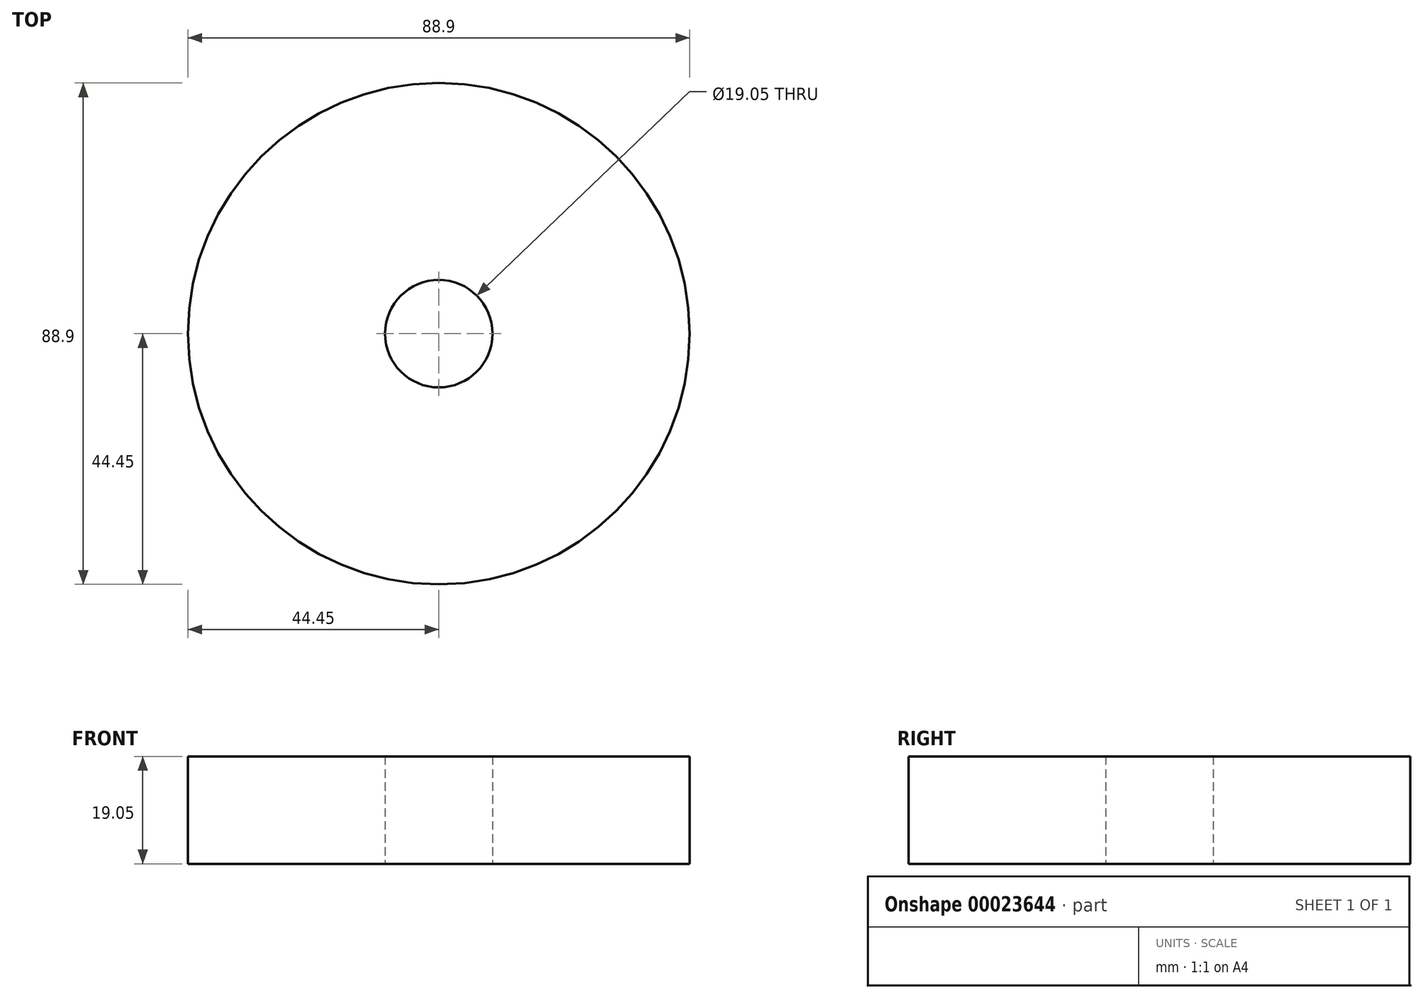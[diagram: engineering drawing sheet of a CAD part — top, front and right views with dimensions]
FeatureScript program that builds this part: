
annotation { "Feature Type Name" : "Feature", "Feature Type Description" : "" }
export const myFeature = defineFeature(function(context is Context, id is Id, definition is map)
    precondition{}
    {
        {
            var Q0;
            Q0=qCreatedBy(makeId("Front.planeOp"),FACE);
            var sketch = newSketch(context, id + "F0", { "sketchPlane" : qUnion([Q0])});
            skLineSegment(sketch, "E0", {"start": v(0, 0) * mm, "end": v(0, 75) * mm, "construction": true});
            skLineSegment(sketch, "E1.bottom", {"start": v(-9.52, 4.98) * mm, "end": v(-44.45, 4.98) * mm});
            skLineSegment(sketch, "E1.top", {"start": v(-9.53, 24.03) * mm, "end": v(-44.45, 24.03) * mm});
            skLineSegment(sketch, "E1.left", {"start": v(-9.53, 4.98) * mm, "end": v(-9.53, 24.03) * mm});
            skLineSegment(sketch, "E1.right", {"start": v(-44.45, 4.98) * mm, "end": v(-44.45, 24.03) * mm});
            skLineSegment(sketch, "E2.bottom", {"start": v(-9.53, 24.03) * mm, "end": v(-25.4, 24.03) * mm});
            skLineSegment(sketch, "E2.top", {"start": v(-9.53, 81.18) * mm, "end": v(-25.4, 81.18) * mm});
            skLineSegment(sketch, "E2.left", {"start": v(-9.53, 24.03) * mm, "end": v(-9.53, 81.18) * mm});
            skLineSegment(sketch, "E2.right", {"start": v(-25.4, 24.03) * mm, "end": v(-25.4, 81.18) * mm});
            skLineSegment(sketch, "E3.bottom", {"start": v(-9.53, 81.18) * mm, "end": v(-19.05, 81.18) * mm});
            skLineSegment(sketch, "E3.top", {"start": v(-9.53, 93.88) * mm, "end": v(-19.05, 93.88) * mm});
            skLineSegment(sketch, "E3.left", {"start": v(-9.53, 81.18) * mm, "end": v(-9.53, 93.88) * mm});
            skLineSegment(sketch, "E3.right", {"start": v(-19.05, 81.18) * mm, "end": v(-19.05, 93.88) * mm});
            skSolve(sketch);
        }
        {
            var Q0;
            Q0=makeQuery(id+"F0.imprint","IMPRINT",FACE,{"disambiguationData":[TD([[makeQuery(id+"F0.imprint","IMPRINT",EDGE,{"derivedFrom":sQuery(id+"F0.wireOp",EDGE,"E3.bottom")}),-1.0]])]});
            var Q1;
            Q1=makeQuery(id+"F0.imprint","IMPRINT",FACE,{"disambiguationData":[TD([[makeQuery(id+"F0.imprint","IMPRINT",EDGE,{"derivedFrom":sQuery(id+"F0.wireOp",EDGE,"E2.bottom")}),-1.0]])]});
            var Q2;
            Q2=makeQuery(id+"F0.imprint","IMPRINT",FACE,{"disambiguationData":[TD([[makeQuery(id+"F0.imprint","IMPRINT",EDGE,{"derivedFrom":sQuery(id+"F0.wireOp",EDGE,"E1.bottom")}),-1.0]])]});
            var Q3;
            Q3=sQuery(id+"F0.wireOp",EDGE,"E0");
            revolve(context, id + "F1", {"entities" : qUnion([Q0, Q1, Q2]), "axis" : qUnion([Q3]), "revolveType" : RevolveType.FULL});
        }
    });
